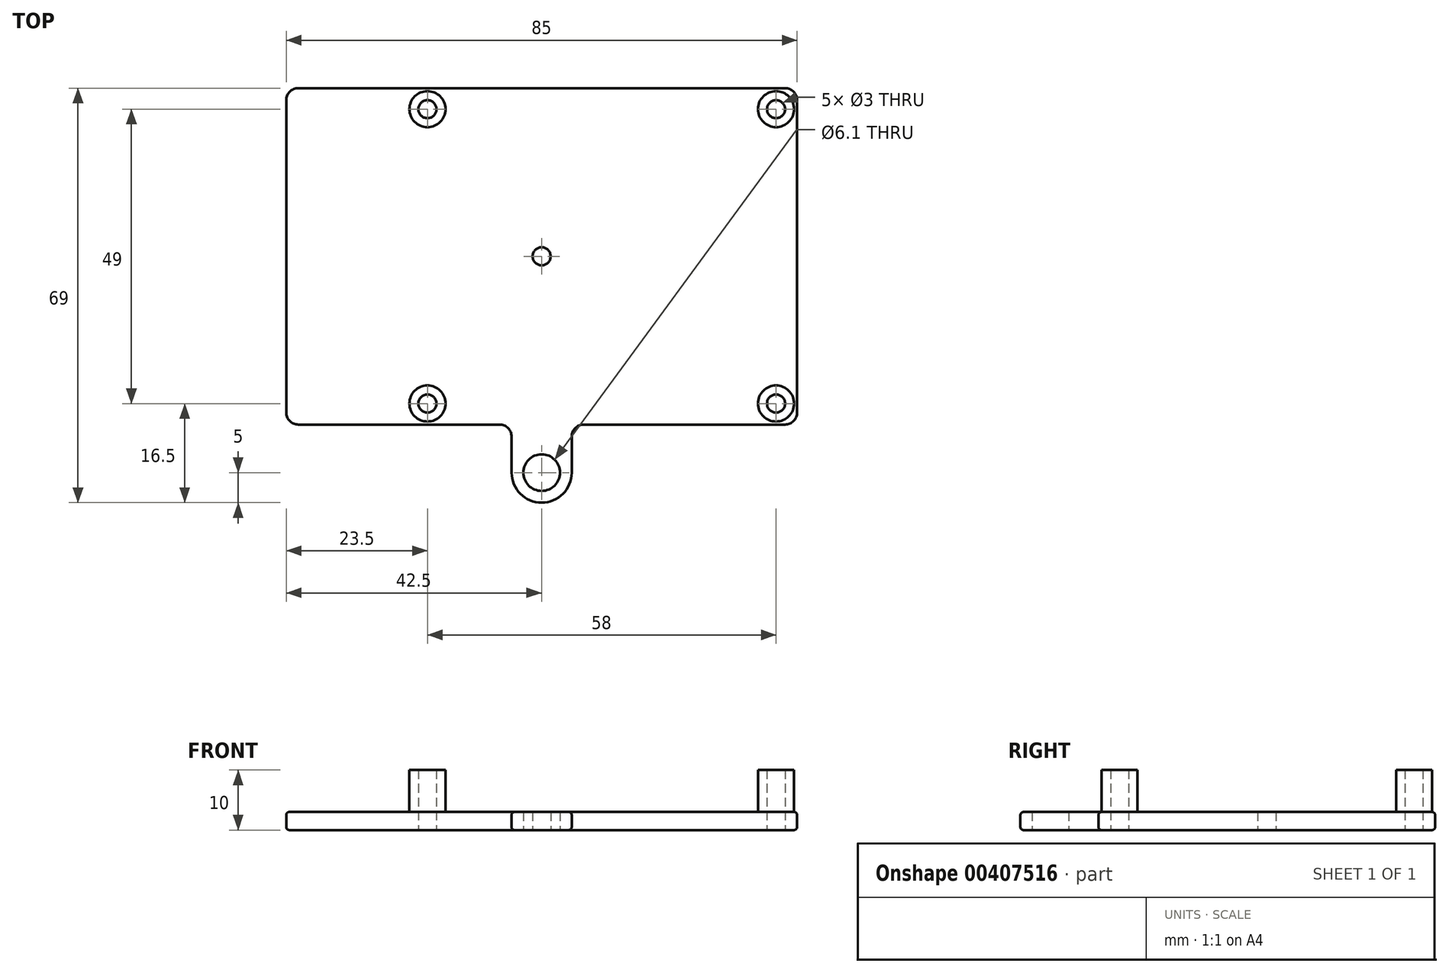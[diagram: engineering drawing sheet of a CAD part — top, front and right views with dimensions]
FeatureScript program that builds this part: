
annotation { "Feature Type Name" : "Feature", "Feature Type Description" : "" }
export const myFeature = defineFeature(function(context is Context, id is Id, definition is map)
    precondition{}
    {
        {
            var Q0;
            Q0=qCreatedBy(makeId("Top.planeOp"),FACE);
            var sketch = newSketch(context, id + "F0", { "sketchPlane" : qUnion([Q0])});
            skLineSegment(sketch, "E0.bottom", {"start": v(40.5, 28) * mm, "end": v(-40.5, 28) * mm});
            skLineSegment(sketch, "E0.top", {"start": v(40.5, -28) * mm, "end": v(7, -28) * mm});
            skLineSegment(sketch, "E0.left", {"start": v(42.5, 26) * mm, "end": v(42.5, -26) * mm});
            skLineSegment(sketch, "E0.right", {"start": v(-42.5, 26) * mm, "end": v(-42.5, -26) * mm});
            skPoint(sketch, "E0.middle", {"position": v(0, 0) * mm});
            skCircle(sketch, "E1", {"center": v(39, -24.5) * mm, "radius": 1.5 * mm});
            skCircle(sketch, "E2", {"center": v(39, 24.5) * mm, "radius": 1.5 * mm});
            skCircle(sketch, "E3", {"center": v(-19, 24.5) * mm, "radius": 1.5 * mm});
            skCircle(sketch, "E4", {"center": v(-19, -24.5) * mm, "radius": 1.5 * mm});
            skCircle(sketch, "E5", {"center": v(0, 0) * mm, "radius": 1.5 * mm});
            skCircle(sketch, "E6", {"center": v(39, -24.5) * mm, "radius": 3 * mm});
            skCircle(sketch, "E7", {"center": v(-19, -24.5) * mm, "radius": 3 * mm});
            skCircle(sketch, "E8", {"center": v(-19, 24.5) * mm, "radius": 3 * mm});
            skCircle(sketch, "E9", {"center": v(39, 24.5) * mm, "radius": 3 * mm});
            skPoint(sketch, "E10.visualSharp", {"position": v(-42.5, 28) * mm});
            skArc(sketch, "E10.filletArc", {"start": v(-40.5, 28) * mm, "mid": v(-41.91, 27.41) * mm, "end": v(-42.5, 26) * mm});
            skPoint(sketch, "E11.visualSharp", {"position": v(42.5, 28) * mm});
            skArc(sketch, "E11.filletArc", {"start": v(42.5, 26) * mm, "mid": v(41.91, 27.41) * mm, "end": v(40.5, 28) * mm});
            skPoint(sketch, "E12.visualSharp", {"position": v(42.5, -28) * mm});
            skArc(sketch, "E12.filletArc", {"start": v(40.5, -28) * mm, "mid": v(41.91, -27.41) * mm, "end": v(42.5, -26) * mm});
            skPoint(sketch, "E13.visualSharp", {"position": v(-42.5, -28) * mm});
            skArc(sketch, "E13.filletArc", {"start": v(-42.5, -26) * mm, "mid": v(-41.91, -27.41) * mm, "end": v(-40.5, -28) * mm});
            skLineSegment(sketch, "E14", {"start": v(0, 0) * mm, "end": v(0, -48.48) * mm, "construction": true});
            skCircle(sketch, "E15", {"center": v(0, -36) * mm, "radius": 3.05 * mm});
            skLineSegment(sketch, "E16", {"start": v(0, -36) * mm, "end": v(15.36, -36) * mm, "construction": true});
            skLineSegment(sketch, "E17", {"start": v(0, -36) * mm, "end": v(-12.46, -36) * mm, "construction": true});
            skArc(sketch, "E18", {"start": v(-5, -36) * mm, "mid": v(0, -41) * mm, "end": v(5, -36) * mm});
            skLineSegment(sketch, "E19", {"start": v(5, -36) * mm, "end": v(5, -30) * mm});
            skLineSegment(sketch, "E20", {"start": v(-5, -36) * mm, "end": v(-5, -30) * mm});
            skLineSegment(sketch, "E21", {"start": v(-7, -28) * mm, "end": v(-40.5, -28) * mm});
            skPoint(sketch, "E22.visualSharp", {"position": v(-5, -28) * mm});
            skArc(sketch, "E22.filletArc", {"start": v(-5, -30) * mm, "mid": v(-5.59, -28.59) * mm, "end": v(-7, -28) * mm});
            skPoint(sketch, "E23.visualSharp", {"position": v(5, -28) * mm});
            skArc(sketch, "E23.filletArc", {"start": v(7, -28) * mm, "mid": v(5.59, -28.59) * mm, "end": v(5, -30) * mm});
            skSolve(sketch);
        }
        {
            var Q0;
            Q0=makeQuery(id+"F0.imprint","IMPRINT",FACE,{"disambiguationData":[TD([[makeQuery(id+"F0.imprint","IMPRINT",EDGE,{"derivedFrom":sQuery(id+"F0.wireOp",EDGE,"E0.bottom")}),1.0]])]});
            var Q1;
            Q1=makeQuery(id+"F0.imprint","IMPRINT",FACE,{"disambiguationData":[TD([[makeQuery(id+"F0.imprint","IMPRINT",EDGE,{"derivedFrom":sQuery(id+"F0.wireOp",EDGE,"UPEMqtsX-Wj4u-wqR3-wpu7-ZDmcPFnyfZg4.bottom")}),-1.0]])]});
            extrude(context, id + "F1", {"entities" : qUnion([Q0, Q1]), "depth" : 3 * mm});
        }
        {
            var Q0;
            Q0=makeQuery(id+"F0.imprint","IMPRINT",FACE,{"disambiguationData":[TD([[makeQuery(id+"F0.imprint","IMPRINT",EDGE,{"derivedFrom":sQuery(id+"F0.wireOp",EDGE,"E4")}),-1.0]])]});
            var Q1;
            Q1=makeQuery(id+"F0.imprint","IMPRINT",FACE,{"disambiguationData":[TD([[makeQuery(id+"F0.imprint","IMPRINT",EDGE,{"derivedFrom":sQuery(id+"F0.wireOp",EDGE,"E3")}),-1.0]])]});
            var Q2;
            Q2=makeQuery(id+"F0.imprint","IMPRINT",FACE,{"disambiguationData":[TD([[makeQuery(id+"F0.imprint","IMPRINT",EDGE,{"derivedFrom":sQuery(id+"F0.wireOp",EDGE,"E2")}),-1.0]])]});
            var Q3;
            Q3=makeQuery(id+"F0.imprint","IMPRINT",FACE,{"disambiguationData":[TD([[makeQuery(id+"F0.imprint","IMPRINT",EDGE,{"derivedFrom":sQuery(id+"F0.wireOp",EDGE,"E1")}),-1.0]])]});
            extrude(context, id + "F2", {"entities" : qUnion([Q0, Q1, Q2, Q3]), "operationType" : NewBodyOperationType.ADD, "depth" : 10 * mm});
        }
        {
            var Q0;
            Q0=makeQuery(id+"F1.opExtrude","CAP_EDGE",EDGE,{"disambiguationData":[OSD([sQuery(id+"F0.wireOp",EDGE,"E0.top")])],"isStart":false});
            var Q1;
            Q1=makeQuery(id+"F1.opExtrude","CAP_EDGE",EDGE,{"disambiguationData":[OSD([sQuery(id+"F0.wireOp",EDGE,"E0.top")])],"isStart":true});
            fillet(context, id + "F3", {"entities" : qUnion([Q0, Q1]), "radius" : 0.5 * mm, "tangentPropagation" : true, "allowEdgeOverflow" : false});
        }
    });
